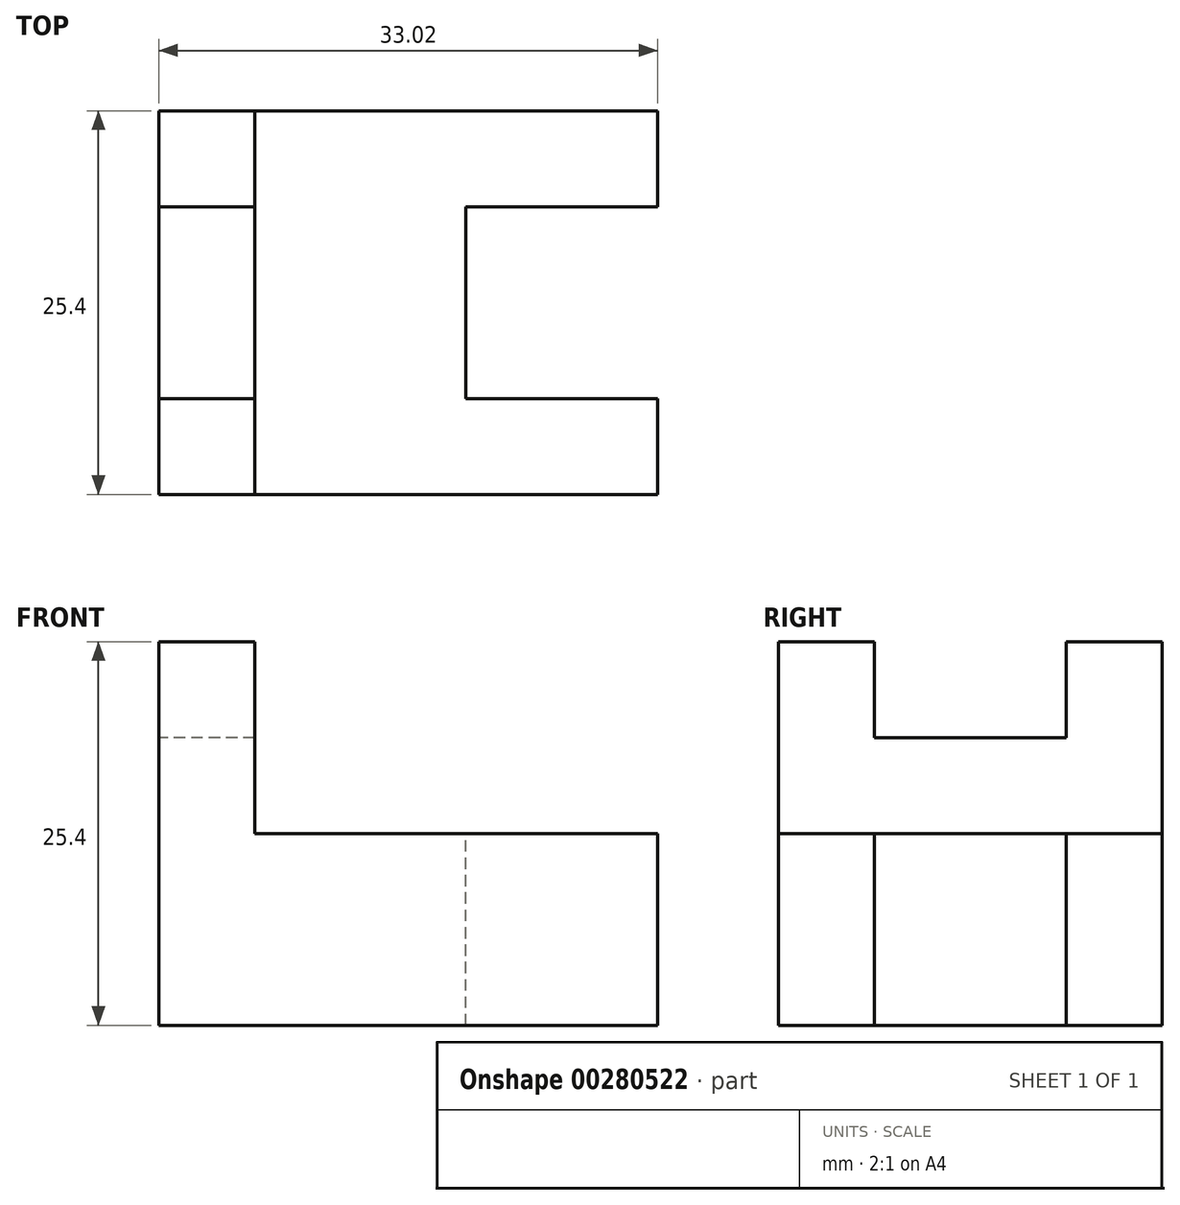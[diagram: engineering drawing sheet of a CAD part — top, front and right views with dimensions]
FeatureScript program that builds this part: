
annotation { "Feature Type Name" : "Feature", "Feature Type Description" : "" }
export const myFeature = defineFeature(function(context is Context, id is Id, definition is map)
    precondition{}
    {
        {
            var Q0;
            Q0=qCreatedBy(makeId("Front.planeOp"),FACE);
            var sketch = newSketch(context, id + "F0", { "sketchPlane" : qUnion([Q0])});
            skLineSegment(sketch, "E0", {"start": v(0, 0) * mm, "end": v(0, 25.4) * mm});
            skLineSegment(sketch, "E1", {"start": v(0, 25.4) * mm, "end": v(6.35, 25.4) * mm});
            skLineSegment(sketch, "E2", {"start": v(6.35, 25.4) * mm, "end": v(6.35, 12.7) * mm});
            skLineSegment(sketch, "E3", {"start": v(6.35, 12.7) * mm, "end": v(33.02, 12.7) * mm});
            skLineSegment(sketch, "E4", {"start": v(33.02, 12.7) * mm, "end": v(33.02, 0) * mm});
            skLineSegment(sketch, "E5", {"start": v(33.02, 0) * mm, "end": v(0, 0) * mm});
            skSolve(sketch);
        }
        {
            var Q0;
            Q0=makeQuery(id+"F0.imprint","IMPRINT",FACE,{"disambiguationData":[TD([[makeQuery(id+"F0.imprint","IMPRINT",EDGE,{"derivedFrom":sQuery(id+"F0.wireOp",EDGE,"E0")}),-1.0]])]});
            extrude(context, id + "F1", {"entities" : qUnion([Q0]), "depth" : 25.4 * mm});
        }
        {
            var Q0;
            Q0=makeQuery(id+"F1.opExtrude","SWEPT_FACE",FACE,{"disambiguationData":[OSD([sQuery(id+"F0.wireOp",EDGE,"E3")])]});
            var sketch = newSketch(context, id + "F2", { "sketchPlane" : qUnion([Q0])});
            skLineSegment(sketch, "E6.bottom", {"start": v(33.02, -6.35) * mm, "end": v(20.32, -6.35) * mm});
            skLineSegment(sketch, "E6.top", {"start": v(33.02, -19.05) * mm, "end": v(20.32, -19.05) * mm});
            skLineSegment(sketch, "E6.left", {"start": v(33.02, -6.35) * mm, "end": v(33.02, -19.05) * mm});
            skLineSegment(sketch, "E6.right", {"start": v(20.32, -6.35) * mm, "end": v(20.32, -19.05) * mm});
            skSolve(sketch);
        }
        {
            var Q0;
            Q0=makeQuery(id+"F2.imprint","IMPRINT",FACE,{"disambiguationData":[TD([[makeQuery(id+"F2.imprint","IMPRINT",EDGE,{"derivedFrom":sQuery(id+"F2.wireOp",EDGE,"E6.bottom")}),1.0]])]});
            extrude(context, id + "F3", {"entities" : qUnion([Q0]), "operationType" : NewBodyOperationType.REMOVE, "endBound" : BoundingType.THROUGH_ALL, "oppositeDirection" : true, "depth" : 25.4 * mm});
        }
        {
            var Q0;
            Q0=makeQuery(id+"F1.opExtrude","SWEPT_FACE",FACE,{"disambiguationData":[OSD([sQuery(id+"F0.wireOp",EDGE,"E1")])]});
            var sketch = newSketch(context, id + "F4", { "sketchPlane" : qUnion([Q0])});
            skLineSegment(sketch, "E7.bottom", {"start": v(6.35, -6.35) * mm, "end": v(0, -6.35) * mm});
            skLineSegment(sketch, "E7.top", {"start": v(6.35, -19.05) * mm, "end": v(0, -19.05) * mm});
            skLineSegment(sketch, "E7.left", {"start": v(6.35, -6.35) * mm, "end": v(6.35, -19.05) * mm});
            skLineSegment(sketch, "E7.right", {"start": v(0, -6.35) * mm, "end": v(0, -19.05) * mm});
            skSolve(sketch);
        }
        {
            var Q0;
            Q0=makeQuery(id+"F4.imprint","IMPRINT",FACE,{"disambiguationData":[TD([[makeQuery(id+"F4.imprint","IMPRINT",EDGE,{"derivedFrom":sQuery(id+"F4.wireOp",EDGE,"E7.bottom")}),1.0]])]});
            extrude(context, id + "F5", {"entities" : qUnion([Q0]), "operationType" : NewBodyOperationType.REMOVE, "oppositeDirection" : true, "depth" : 6.35 * mm});
        }
    });
